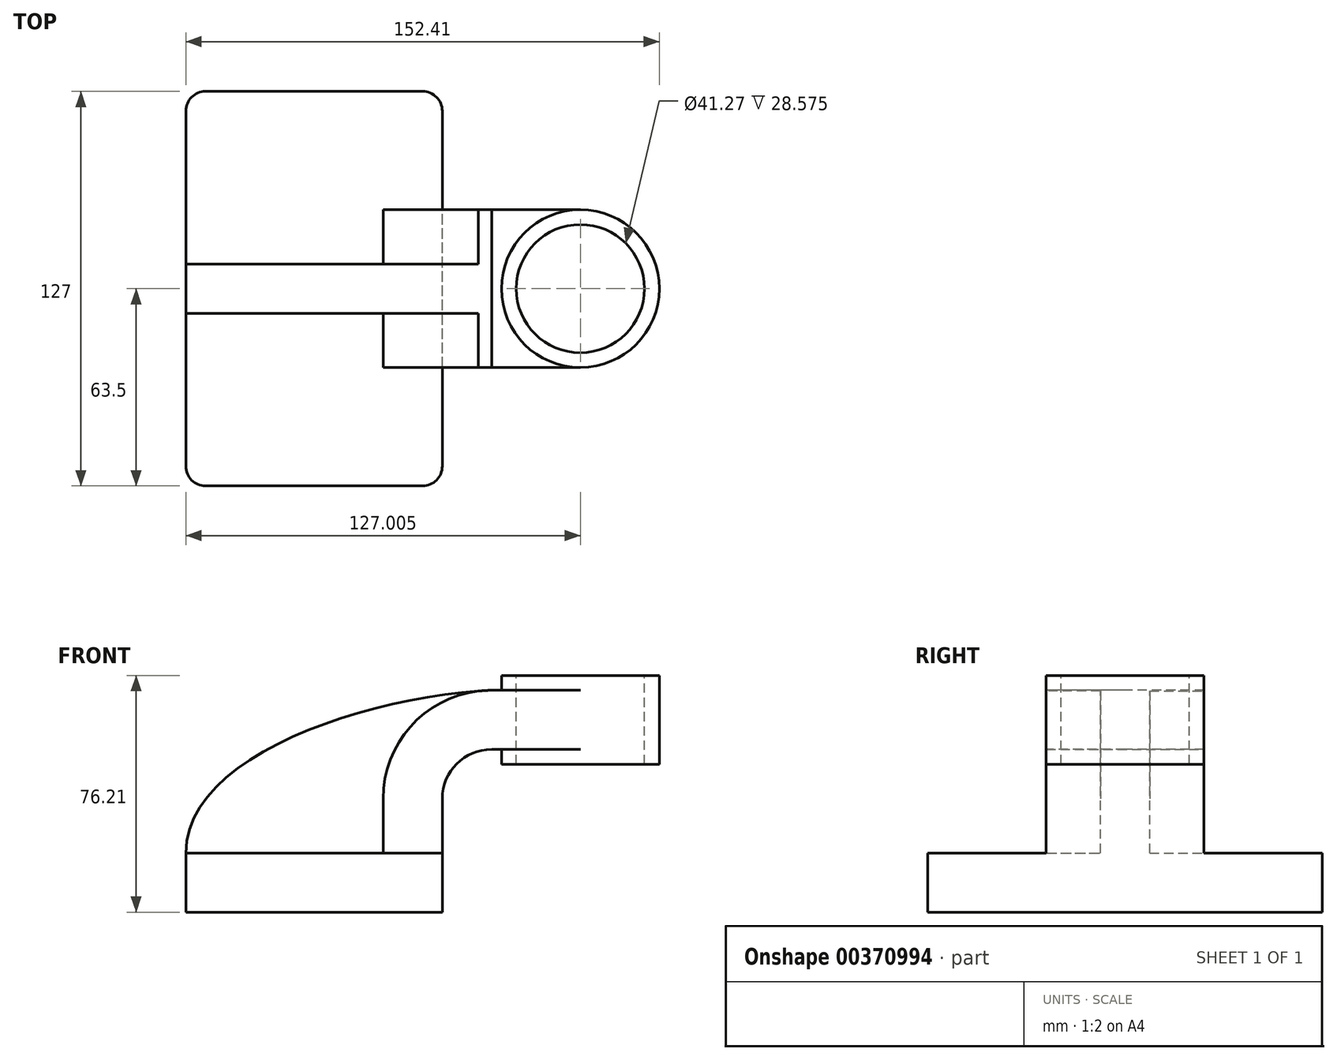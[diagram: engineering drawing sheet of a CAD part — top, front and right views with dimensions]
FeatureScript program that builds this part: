
annotation { "Feature Type Name" : "Feature", "Feature Type Description" : "" }
export const myFeature = defineFeature(function(context is Context, id is Id, definition is map)
    precondition{}
    {
        {
            var Q0;
            Q0=qCreatedBy(makeId("Front.planeOp"),FACE);
            var sketch = newSketch(context, id + "F0", { "sketchPlane" : qUnion([Q0])});
            skLineSegment(sketch, "E0.bottom", {"start": v(-41.28, 9.53) * mm, "end": v(41.28, 9.53) * mm});
            skLineSegment(sketch, "E0.top", {"start": v(-41.28, -9.53) * mm, "end": v(41.28, -9.53) * mm});
            skLineSegment(sketch, "E0.left", {"start": v(-41.27, 9.52) * mm, "end": v(-41.27, -9.53) * mm});
            skLineSegment(sketch, "E0.right", {"start": v(41.28, 9.53) * mm, "end": v(41.28, -9.52) * mm});
            skPoint(sketch, "E0.middle", {"position": v(0, 0) * mm});
            skLineSegment(sketch, "E1.bottom", {"start": v(60.32, 66.67) * mm, "end": v(111.13, 66.68) * mm});
            skLineSegment(sketch, "E1.top", {"start": v(60.33, 38.1) * mm, "end": v(111.13, 38.1) * mm});
            skLineSegment(sketch, "E1.left", {"start": v(60.32, 66.67) * mm, "end": v(60.32, 38.1) * mm});
            skLineSegment(sketch, "E1.right", {"start": v(111.13, 66.67) * mm, "end": v(111.13, 38.1) * mm});
            skPoint(sketch, "E1.middle", {"position": v(85.73, 52.39) * mm});
            skLineSegment(sketch, "E2", {"start": v(41.28, 9.53) * mm, "end": v(41.28, 26.99) * mm});
            skArc(sketch, "E3", {"start": v(57.15, 42.86) * mm, "mid": v(45.92, 38.21) * mm, "end": v(41.27, 26.99) * mm});
            skLineSegment(sketch, "E4", {"start": v(57.15, 42.86) * mm, "end": v(85.72, 42.86) * mm});
            skLineSegment(sketch, "E5.0", {"start": v(57.15, 61.91) * mm, "end": v(85.73, 61.91) * mm});
            skArc(sketch, "E5.1", {"start": v(57.15, 61.91) * mm, "mid": v(32.45, 51.68) * mm, "end": v(22.22, 26.99) * mm});
            skLineSegment(sketch, "E5.2", {"start": v(22.22, 9.52) * mm, "end": v(22.22, 26.99) * mm});
            skLineSegment(sketch, "E6", {"start": v(85.73, 38.1) * mm, "end": v(85.73, 66.67) * mm});
            skFitSpline(sketch, "E7", {"points": [v(-41.27, 9.52) * mm, v(57.15, 61.91) * mm], "startDerivative": vector(0, 93.72) * mm, "endDerivative": vector(122.12, 5.87) * mm});
            skSolve(sketch);
        }
        {
            var Q0;
            Q0=makeQuery(id+"F0.imprint","IMPRINT",FACE,{"disambiguationData":[TD([[makeQuery(id+"F0.imprint","IMPRINT",EDGE,{"derivedFrom":sQuery(id+"F0.wireOp",EDGE,"E0.bottom")}),-1.0]])]});
            extrude(context, id + "F1", {"entities" : qUnion([Q0]), "endBound" : BoundingType.SYMMETRIC, "depth" : 127 * mm});
        }
        {
            var Q0;
            {var subQ1=sQuery(id+"F0.wireOp",EDGE,"E2");Q0=makeQuery(id+"F0.imprint","IMPRINT",FACE,{"disambiguationData":[TD([[makeQuery(id+"F0.imprint","IMPRINT",EDGE,{"derivedFrom":subQ1}),1.0]])]});}
            var Q1;
            {var subQ0=sQuery(id+"F0.wireOp",EDGE,"E5.0");var subQ1=sQuery(id+"F0.wireOp",EDGE,"E1.left");var subQ2=makeQuery(id+"F0.imprint","INTERSECT",VERTEX,{"derivedFrom":[subQ1,subQ0]});Q1=makeQuery(id+"F0.imprint","IMPRINT",FACE,{"disambiguationData":[TD([[makeQuery(id+"F0.imprint","IMPRINT",EDGE,{"disambiguationData":[TD([[subQ2,-1.0]])],"derivedFrom":subQ1}),1.0]])]});}
            extrude(context, id + "F2", {"entities" : qUnion([Q0, Q1]), "operationType" : NewBodyOperationType.ADD, "endBound" : BoundingType.SYMMETRIC, "depth" : 50.8 * mm});
        }
        {
            var Q0;
            Q0=makeQuery(id+"F0.imprint","IMPRINT",FACE,{"disambiguationData":[TD([[makeQuery(id+"F0.imprint","IMPRINT",EDGE,{"derivedFrom":sQuery(id+"F0.wireOp",EDGE,"E5.1")}),-1.0]])]});
            extrude(context, id + "F3", {"entities" : qUnion([Q0]), "operationType" : NewBodyOperationType.ADD, "endBound" : BoundingType.SYMMETRIC, "depth" : 15.88 * mm});
        }
        {
            var Q0;
            {var subQ0=sQuery(id+"F0.wireOp",EDGE,"E1.right");Q0=makeQuery(id+"F0.imprint","IMPRINT",FACE,{"disambiguationData":[TD([[makeQuery(id+"F0.imprint","IMPRINT",EDGE,{"derivedFrom":subQ0}),-1.0]])]});}
            var Q1;
            Q1=sQuery(id+"F0.wireOp",EDGE,"E6");
            revolve(context, id + "F4", {"operationType" : NewBodyOperationType.ADD, "entities" : qUnion([Q0]), "axis" : qUnion([Q1]), "revolveType" : RevolveType.FULL});
        }
        {
            var Q0;
            Q0=makeQuery(id+"F1.opExtrude","CAP_EDGE",EDGE,{"disambiguationData":[OSD([sQuery(id+"F0.wireOp",EDGE,"E0.right")])],"isStart":false});
            var Q1;
            Q1=makeQuery(id+"F1.opExtrude","CAP_EDGE",EDGE,{"disambiguationData":[OSD([sQuery(id+"F0.wireOp",EDGE,"E0.left")])],"isStart":false});
            var Q2;
            Q2=makeQuery(id+"F1.opExtrude","CAP_EDGE",EDGE,{"disambiguationData":[OSD([sQuery(id+"F0.wireOp",EDGE,"E0.right")])],"isStart":true});
            var Q3;
            Q3=makeQuery(id+"F1.opExtrude","CAP_EDGE",EDGE,{"disambiguationData":[OSD([sQuery(id+"F0.wireOp",EDGE,"E0.left")])],"isStart":true});
            fillet(context, id + "F5", {"entities" : qUnion([Q0, Q1, Q2, Q3]), "radius" : 6.35 * mm, "tangentPropagation" : true, "allowEdgeOverflow" : false});
        }
        {
            var Q0;
            Q0=makeQuery(id+"F4.opRevolve","SWEPT_FACE",FACE,{"disambiguationData":[OSD([sQuery(id+"F0.wireOp",EDGE,"E1.bottom")])]});
            var sketch = newSketch(context, id + "F6", { "sketchPlane" : qUnion([Q0])});
            skCircle(sketch, "E8", {"center": v(85.73, 0) * mm, "radius": 20.64 * mm});
            skSolve(sketch);
        }
        {
            var Q0;
            Q0=makeQuery(id+"F6.imprint","IMPRINT",FACE,{"disambiguationData":[TD([[makeQuery(id+"F6.imprint","IMPRINT",EDGE,{"derivedFrom":sQuery(id+"F6.wireOp",EDGE,"E8")}),1.0]])]});
            var Q1;
            Q1=sQuery(id+"F6.wireOp",EDGE,"E8");
            extrude(context, id + "F7", {"entities" : qUnion([Q0]), "operationType" : NewBodyOperationType.REMOVE, "surfaceEntities" : qUnion([Q1]), "endBound" : BoundingType.UP_TO_NEXT, "oppositeDirection" : true, "depth" : 25.4 * mm});
        }
    });
